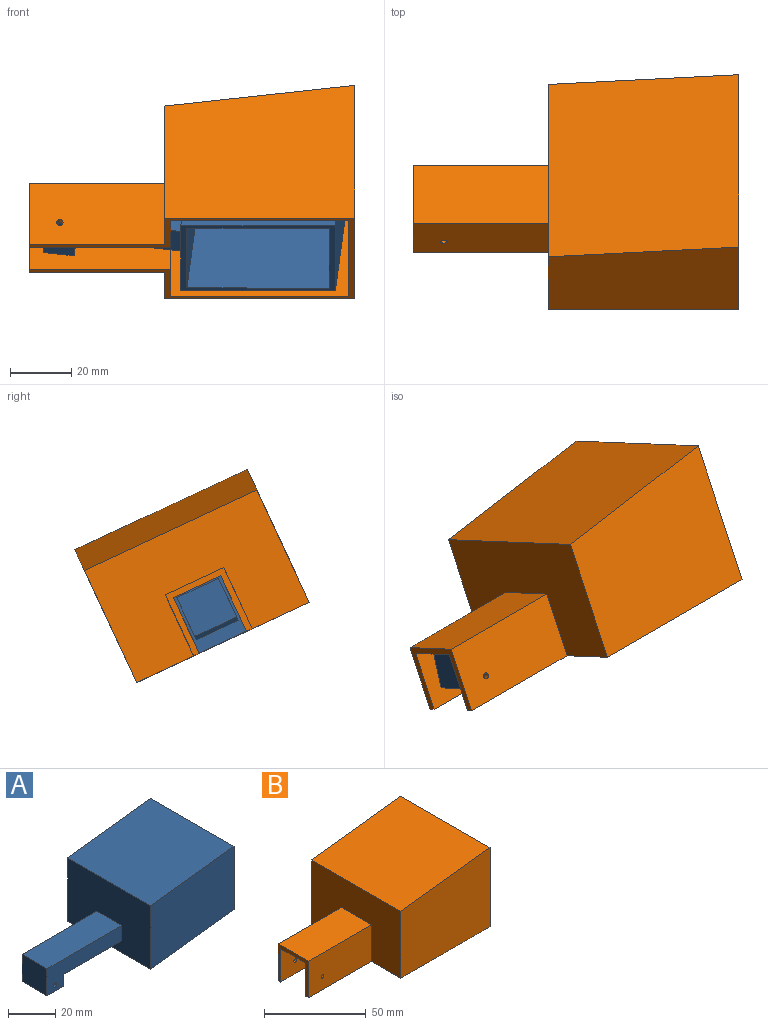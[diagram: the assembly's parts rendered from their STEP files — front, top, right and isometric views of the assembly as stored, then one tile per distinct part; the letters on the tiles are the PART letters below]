
ASSEMBLY  parts=2 mates=1
PART A: 25 faces, bbox 95x50x39 mm
  f0: plane 50x33mm, normal (-1,0,0), area 1530mm2, adj f1,f2,f4,f5,f6,f7,f8,f17
  f1: plane 50x39mm, normal (0,-1,0), area 1650mm2, adj f0,f3,f8,f17
  f2: plane 50x39mm, normal (0,1,0), area 1650mm2, adj f0,f3,f8,f17
  f3: plane 50x33mm, normal (1,0,0), area 1650mm2, adj f1,f2,f8,f17
  f4: plane 35x15mm, normal (0,0,-1), area 525mm2, adj f0,f5,f7,f15
  f5: plane 45x14mm, normal (0,-1,0), area 416.9mm2, adj f0,f4,f6,f13,f14,f15,f18
  f6: plane 45x15mm, normal (0,0,1), area 675mm2, adj f0,f5,f7,f14
  f7: plane 45x14mm, normal (0,1,0), area 416.9mm2, adj f0,f4,f6,f13,f14,f15,f18
  f8: plane 50x50mm, normal (0.12,0,-0.99), area 386.8mm2, adj f0,f1,f2,f3,f9,f10,f11,f12
  f9: plane 46x31mm, normal (-1,0,0), area 1426mm2, adj f8,f10,f12,f16
  f10: plane 46x36.52mm, normal (0,-1,0), area 1426mm2, adj f8,f9,f11,f16
  f11: plane 46x31mm, normal (1,0,0), area 1426mm2, adj f8,f10,f12,f16
  f12: plane 46x36.52mm, normal (0,1,0), area 1426mm2, adj f8,f9,f11,f16
  f13: plane 15x10mm, normal (0,0,-1), area 150mm2, adj f5,f7,f14,f15
  f14: plane 15x14mm, normal (-1,0,0), area 210mm2, adj f5,f6,f7,f13
  f15: plane 15x6mm, normal (1,0,0), area 90mm2, adj f4,f5,f7,f13
  f16: plane 46x46mm, normal (0.12,0,-0.99), area 2131.2mm2, adj f9,f10,f11,f12
  f17: plane 50x50mm, normal (-0.12,0,0.99), area 2517.9mm2, adj f0,f1,f2,f3
  f18: cylinder r=1mm len=15mm, axis (0,1,0), area 94.2mm2, adj f5,f7
  f19: plane 11x4mm, normal (-1,0,0), area 44mm2, adj f20,f21,f22,f23
  f20: plane 35x4mm, normal (0,1,0), area 140mm2, adj f19,f21,f23,f24
  f21: plane 35x11mm, normal (0,0,-1), area 385mm2, adj f19,f20,f22,f24
  f22: plane 35x4mm, normal (0,-1,0), area 140mm2, adj f19,f21,f23,f24
  f23: plane 35x11mm, normal (0,0,1), area 385mm2, adj f19,f20,f22,f24
  f24: plane 11x4mm, normal (1,0,0), area 44mm2, adj f20,f21,f22,f23
PART B: 20 faces, bbox 106x62x47.7 mm
  f0: plane 58x38.52mm, normal (1,0,0), area 1894.2mm2, adj f2,f3,f4,f9,f11,f12,f13
  f1: plane 62x40.28mm, normal (-1,0,0), area 2035.4mm2, adj f5,f7,f9,f10,f15,f16,f17
  f2: plane 58x58mm, normal (0.12,0,-0.99), area 3388.1mm2, adj f0,f3,f4,f8
  f3: plane 58x45.48mm, normal (0,1,0), area 2436mm2, adj f0,f2,f8,f9
  f4: plane 58x45.48mm, normal (0,-1,0), area 2436mm2, adj f0,f2,f8,f9
  f5: plane 62x47.72mm, normal (0,-1,0), area 2728mm2, adj f1,f6,f9,f10
  f6: plane 62x47.72mm, normal (1,0,0), area 2958.6mm2, adj f5,f7,f9,f10
  f7: plane 62x47.72mm, normal (0,1,0), area 2728mm2, adj f1,f6,f9,f10
  f8: plane 58x45.48mm, normal (-1,0,0), area 2637.8mm2, adj f2,f3,f4,f9
  f9: plane 106x62mm, normal (0,0,-1), area 622mm2, adj f0,f1,f3,f4,f5,f6,f7,f8
  f10: plane 62x62mm, normal (-0.12,0,0.99), area 3871.6mm2, adj f1,f5,f6,f7
  f11: plane 46x20mm, normal (0,1,0), area 916.9mm2, adj f0,f9,f12,f14,f19
  f12: plane 46x17mm, normal (0,0,-1), area 782mm2, adj f0,f11,f13,f14
  f13: plane 46x20mm, normal (0,-1,0), area 916.9mm2, adj f0,f9,f12,f14,f18
  f14: plane 22x21mm, normal (-1,0,0), area 122mm2, adj f9,f11,f12,f13,f15,f16,f17
  f15: plane 44x22mm, normal (0,-1,0), area 964.9mm2, adj f1,f9,f14,f17,f19
  f16: plane 44x22mm, normal (0,1,0), area 964.9mm2, adj f1,f9,f14,f17,f18
  f17: plane 44x21mm, normal (0,0,1), area 924mm2, adj f1,f14,f15,f16
  f18: cylinder r=1mm len=2mm, axis (0,1,0), area 12.6mm2, adj f13,f16
  f19: cylinder r=1mm len=2mm, axis (0,1,0), area 12.6mm2, adj f11,f15
PLACE A rot(axis=(-0.96,0.27,-0.06),25.9deg) t=(-3.78,-14.68,52.72)mm
PLACE B rot(axis=(-1,0,0),25deg) t=(-2.93,-11.34,59.87)mm
MATE revolute A.f18 <-> B.f18  axis (0,-0.91,0.42) through (-67.93,-16.87,65.76)mm
